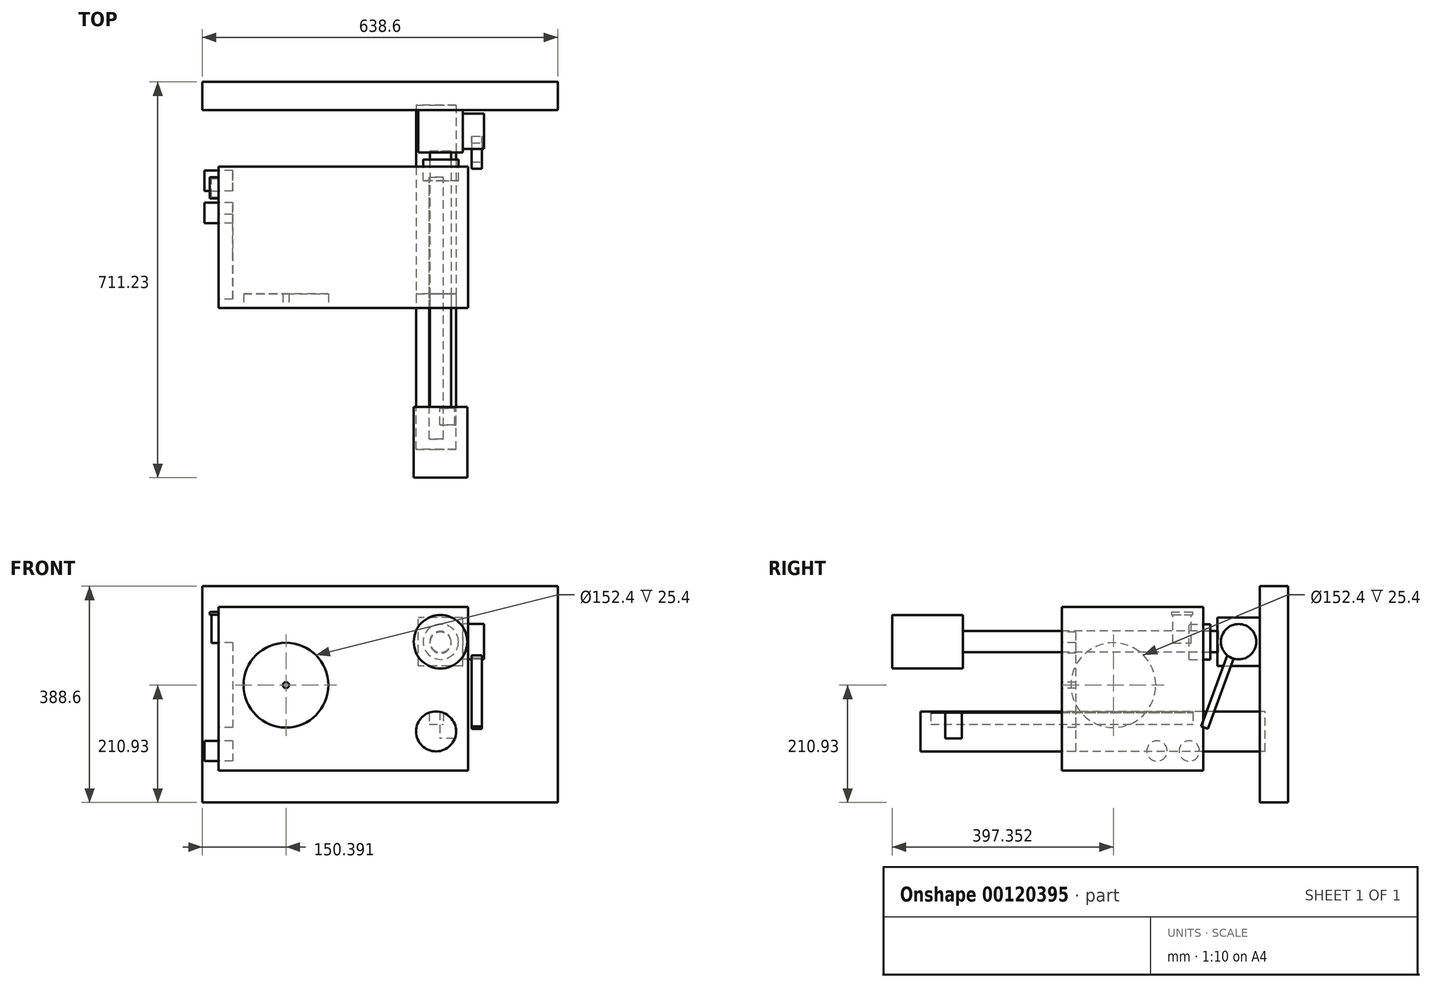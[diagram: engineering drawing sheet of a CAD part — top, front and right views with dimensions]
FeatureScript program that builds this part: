
annotation { "Feature Type Name" : "Feature", "Feature Type Description" : "" }
export const myFeature = defineFeature(function(context is Context, id is Id, definition is map)
    precondition{}
    {
        {
            var Q0;
            Q0=qCreatedBy(makeId("Front.planeOp"),FACE);
            var sketch = newSketch(context, id + "F0", { "sketchPlane" : qUnion([Q0])});
            skLineSegment(sketch, "E0.bottom", {"start": v(319.3, -194.3) * mm, "end": v(-319.3, -194.3) * mm});
            skLineSegment(sketch, "E0.top", {"start": v(319.3, 194.3) * mm, "end": v(-319.3, 194.3) * mm});
            skLineSegment(sketch, "E0.left", {"start": v(319.3, -194.3) * mm, "end": v(319.3, 194.3) * mm});
            skLineSegment(sketch, "E0.right", {"start": v(-319.3, -194.3) * mm, "end": v(-319.3, 194.3) * mm});
            skPoint(sketch, "E0.middle", {"position": v(0, 0) * mm});
            skSolve(sketch);
        }
        {
            var Q0;
            Q0 = qSketchRegion(id + "F0", true);
            extrude(context, id + "F1", {"entities" : qUnion([Q0]), "depth" : 50.8 * mm});
        }
        {
            var Q0;
            Q0=makeQuery(id+"F1.opExtrude","CAP_FACE",FACE,{"disambiguationData":[OSD([sQuery(id+"F0.wireOp",EDGE,"E0.bottom"),sQuery(id+"F0.wireOp",EDGE,"E0.top"),sQuery(id+"F0.wireOp",EDGE,"E0.left"),sQuery(id+"F0.wireOp",EDGE,"E0.right")])],"isStart":false});
            var sketch = newSketch(context, id + "F2", { "sketchPlane" : qUnion([Q0])});
            skLineSegment(sketch, "E1.bottom", {"start": v(148.82, 51.23) * mm, "end": v(68.51, 51.23) * mm});
            skLineSegment(sketch, "E1.top", {"start": v(148.82, 137.9) * mm, "end": v(68.51, 137.9) * mm});
            skLineSegment(sketch, "E1.left", {"start": v(148.82, 51.23) * mm, "end": v(148.82, 137.9) * mm});
            skLineSegment(sketch, "E1.right", {"start": v(68.51, 51.23) * mm, "end": v(68.51, 137.9) * mm});
            skPoint(sketch, "E1.middle", {"position": v(108.67, 94.56) * mm});
            skSolve(sketch);
        }
        {
            var Q0;
            Q0 = qSketchRegion(id + "F2", true);
            extrude(context, id + "F3", {"entities" : qUnion([Q0]), "operationType" : NewBodyOperationType.ADD, "depth" : 76.2 * mm});
        }
        {
            var Q0;
            Q0=makeQuery(id+"F3.opExtrude","SWEPT_FACE",FACE,{"disambiguationData":[OSD([sQuery(id+"F2.wireOp",EDGE,"E1.left")])]});
            var sketch = newSketch(context, id + "F4", { "sketchPlane" : qUnion([Q0])});
            skLineSegment(sketch, "E2", {"start": v(-127, 137.9) * mm, "end": v(-50.8, 51.23) * mm, "construction": true});
            skLineSegment(sketch, "E3", {"start": v(-50.8, 137.9) * mm, "end": v(-127, 51.23) * mm, "construction": true});
            skCircle(sketch, "E4", {"center": v(-88.9, 94.56) * mm, "radius": 31.75 * mm});
            skSolve(sketch);
        }
        {
            var Q0;
            Q0 = qSketchRegion(id + "F4", true);
            extrude(context, id + "F5", {"entities" : qUnion([Q0]), "operationType" : NewBodyOperationType.ADD, "depth" : 38.1 * mm});
        }
        {
            var Q0;
            Q0=makeQuery(id+"F3.opExtrude","CAP_FACE",FACE,{"disambiguationData":[OSD([sQuery(id+"F2.wireOp",EDGE,"E1.bottom"),sQuery(id+"F2.wireOp",EDGE,"E1.top"),sQuery(id+"F2.wireOp",EDGE,"E1.left"),sQuery(id+"F2.wireOp",EDGE,"E1.right")])],"isStart":false});
            var sketch = newSketch(context, id + "F6", { "sketchPlane" : qUnion([Q0])});
            skLineSegment(sketch, "E5", {"start": v(68.51, 137.9) * mm, "end": v(148.82, 51.23) * mm, "construction": true});
            skLineSegment(sketch, "E6", {"start": v(148.82, 137.9) * mm, "end": v(68.51, 51.23) * mm, "construction": true});
            skCircle(sketch, "E7", {"center": v(108.67, 94.56) * mm, "radius": 19.05 * mm});
            skSolve(sketch);
        }
        {
            var Q0;
            Q0 = qSketchRegion(id + "F6", true);
            extrude(context, id + "F7", {"entities" : qUnion([Q0]), "operationType" : NewBodyOperationType.ADD, "depth" : 25.4 * mm});
        }
        {
            var Q0;
            Q0=makeQuery(id+"F7.opExtrude","CAP_FACE",FACE,{"disambiguationData":[OSD([sQuery(id+"F6.wireOp",EDGE,"E7")])],"isStart":false});
            var sketch = newSketch(context, id + "F8", { "sketchPlane" : qUnion([Q0])});
            skLineSegment(sketch, "E8.bottom", {"start": v(158.58, 157.17) * mm, "end": v(-289.75, 157.17) * mm});
            skLineSegment(sketch, "E8.top", {"start": v(158.58, -137.04) * mm, "end": v(-289.75, -137.04) * mm});
            skLineSegment(sketch, "E8.left", {"start": v(158.58, 157.17) * mm, "end": v(158.58, -137.04) * mm});
            skLineSegment(sketch, "E8.right", {"start": v(-289.75, 157.17) * mm, "end": v(-289.75, -137.04) * mm});
            skSolve(sketch);
        }
        {
            var Q0;
            Q0 = qSketchRegion(id + "F8", true);
            extrude(context, id + "F9", {"entities" : qUnion([Q0]), "depth" : 254 * mm});
        }
        {
            var Q0;
            Q0=makeQuery(id+"F9.opExtrude","CAP_FACE",FACE,{"disambiguationData":[OSD([sQuery(id+"F8.wireOp",EDGE,"E8.bottom"),sQuery(id+"F8.wireOp",EDGE,"E8.top"),sQuery(id+"F8.wireOp",EDGE,"E8.left"),sQuery(id+"F8.wireOp",EDGE,"E8.right")])],"isStart":false});
            var sketch = newSketch(context, id + "F10", { "sketchPlane" : qUnion([Q0])});
            skCircle(sketch, "E9", {"center": v(-168.9, 16.63) * mm, "radius": 76.2 * mm});
            skCircle(sketch, "E10", {"center": v(-168.9, 16.63) * mm, "radius": 5.36 * mm});
            skCircle(sketch, "E11", {"center": v(108.84, 92.81) * mm, "radius": 19.05 * mm});
            skCircle(sketch, "E12", {"center": v(100.79, -66.56) * mm, "radius": 35.94 * mm});
            skLineSegment(sketch, "E13.bottom", {"start": v(88.35, -23.15) * mm, "end": v(113.75, -23.15) * mm});
            skLineSegment(sketch, "E13.top", {"start": v(88.35, -53.63) * mm, "end": v(113.75, -53.63) * mm});
            skLineSegment(sketch, "E13.left", {"start": v(88.35, -23.15) * mm, "end": v(88.35, -53.63) * mm});
            skLineSegment(sketch, "E13.right", {"start": v(113.75, -23.15) * mm, "end": v(113.75, -53.63) * mm});
            skSolve(sketch);
        }
        {
            var Q0;
            Q0=makeQuery(id+"F9.opExtrude","SWEPT_FACE",FACE,{"disambiguationData":[OSD([sQuery(id+"F8.wireOp",EDGE,"E8.right")])]});
            var sketch = newSketch(context, id + "F11", { "sketchPlane" : qUnion([Q0])});
            skCircle(sketch, "E14", {"center": v(313.88, 16.63) * mm, "radius": 76.2 * mm});
            skCircle(sketch, "E15", {"center": v(177.56, -101.7) * mm, "radius": 18.33 * mm});
            skCircle(sketch, "E16", {"center": v(235.51, -101.7) * mm, "radius": 18.33 * mm});
            skLineSegment(sketch, "E17", {"start": v(177.56, -101.7) * mm, "end": v(235.51, -101.7) * mm, "construction": true});
            skLineSegment(sketch, "E18.bottom", {"start": v(207.08, 92.5) * mm, "end": v(173.8, 92.5) * mm});
            skLineSegment(sketch, "E18.top", {"start": v(207.08, 143.3) * mm, "end": v(173.8, 143.3) * mm});
            skLineSegment(sketch, "E18.left", {"start": v(207.08, 92.5) * mm, "end": v(207.08, 143.3) * mm});
            skLineSegment(sketch, "E18.right", {"start": v(173.8, 92.5) * mm, "end": v(173.8, 143.3) * mm});
            skSolve(sketch);
        }
        {
            var Q0;
            Q0=makeQuery(id+"F10.imprint","IMPRINT",FACE,{"disambiguationData":[TD([[makeQuery(id+"F10.imprint","IMPRINT",EDGE,{"derivedFrom":sQuery(id+"F10.wireOp",EDGE,"E11")}),1.0]])]});
            extrude(context, id + "F12", {"entities" : qUnion([Q0]), "operationType" : NewBodyOperationType.REMOVE, "oppositeDirection" : true, "depth" : 25.4 * mm});
        }
        {
            var Q0;
            Q0=makeQuery(id+"F10.imprint","IMPRINT",FACE,{"disambiguationData":[TD([[makeQuery(id+"F10.imprint","IMPRINT",EDGE,{"derivedFrom":sQuery(id+"F10.wireOp",EDGE,"E12")}),1.0]])]});
            extrude(context, id + "F13", {"entities" : qUnion([Q0]), "operationType" : NewBodyOperationType.REMOVE, "oppositeDirection" : true, "depth" : 25.4 * mm});
        }
        {
            var Q0;
            Q0=makeQuery(id+"F10.imprint","IMPRINT",FACE,{"disambiguationData":[TD([[makeQuery(id+"F10.imprint","IMPRINT",EDGE,{"derivedFrom":sQuery(id+"F10.wireOp",EDGE,"E9")}),1.0]])]});
            extrude(context, id + "F14", {"entities" : qUnion([Q0]), "operationType" : NewBodyOperationType.REMOVE, "oppositeDirection" : true, "depth" : 25.4 * mm});
        }
        {
            var Q0;
            Q0=makeQuery(id+"F11.imprint","IMPRINT",FACE,{"disambiguationData":[TD([[makeQuery(id+"F11.imprint","IMPRINT",EDGE,{"derivedFrom":sQuery(id+"F11.wireOp",EDGE,"E14")}),1.0]])]});
            extrude(context, id + "F15", {"entities" : qUnion([Q0]), "operationType" : NewBodyOperationType.REMOVE, "oppositeDirection" : true, "depth" : 25.4 * mm});
        }
        {
            var Q0;
            Q0=makeQuery(id+"F11.imprint","IMPRINT",FACE,{"disambiguationData":[TD([[makeQuery(id+"F11.imprint","IMPRINT",EDGE,{"derivedFrom":sQuery(id+"F11.wireOp",EDGE,"E16")}),1.0]])]});
            extrude(context, id + "F16", {"entities" : qUnion([Q0]), "operationType" : NewBodyOperationType.REMOVE, "oppositeDirection" : true, "depth" : 25.4 * mm});
        }
        {
            var Q0;
            Q0=makeQuery(id+"F11.imprint","IMPRINT",FACE,{"disambiguationData":[TD([[makeQuery(id+"F11.imprint","IMPRINT",EDGE,{"derivedFrom":sQuery(id+"F11.wireOp",EDGE,"E15")}),1.0]])]});
            extrude(context, id + "F17", {"entities" : qUnion([Q0]), "operationType" : NewBodyOperationType.REMOVE, "oppositeDirection" : true, "depth" : 25.4 * mm});
        }
        {
            var Q0;
            Q0=makeQuery(id+"F9.opExtrude","SWEPT_FACE",FACE,{"disambiguationData":[OSD([sQuery(id+"F8.wireOp",EDGE,"E8.left")])]});
            cPlane(context, id + "F18", {"entities" : qUnion([Q0]), "cplaneType" : CPlaneType.OFFSET, "offset" : 50.8 * mm, "oppositeDirection" : true, "width" : 152.4 * mm, "height" : 152.4 * mm});
        }
        {
            var Q0;
            Q0=qCreatedBy(id+"F18.planeOp",FACE);
            var sketch = newSketch(context, id + "F19", { "sketchPlane" : qUnion([Q0])});
            skLineSegment(sketch, "E19", {"start": v(-632.3, 94.42) * mm, "end": v(-124.3, 94.42) * mm, "construction": true});
            skLineSegment(sketch, "E20", {"start": v(-584.23, 94.42) * mm, "end": v(-124.3, 94.42) * mm});
            skLineSegment(sketch, "E21", {"start": v(-154.6, -67.58) * mm, "end": v(-688, -67.58) * mm});
            skLineSegment(sketch, "E22.bottom", {"start": v(-616.2, -28.57) * mm, "end": v(-586.36, -28.57) * mm});
            skLineSegment(sketch, "E22.top", {"start": v(-616.2, -79.37) * mm, "end": v(-586.36, -79.37) * mm});
            skLineSegment(sketch, "E22.left", {"start": v(-616.2, -28.57) * mm, "end": v(-616.2, -79.37) * mm});
            skLineSegment(sketch, "E22.right", {"start": v(-586.36, -28.57) * mm, "end": v(-586.36, -79.37) * mm});
            skSolve(sketch);
        }
        {
            var Q0;
            Q0 = qSketchRegion(id + "F6", true);
            var Q1;
            Q1=sQuery(id+"F19.wireOp",EDGE,"E20");
            sweep(context, id + "F20", {"profiles" : qUnion([Q0]), "path" : qUnion([Q1])});
        }
        {
            var Q0;
            Q0=makeQuery(id+"F10.imprint","IMPRINT",FACE,{"disambiguationData":[TD([[makeQuery(id+"F10.imprint","IMPRINT",EDGE,{"derivedFrom":sQuery(id+"F10.wireOp",EDGE,"E12")}),1.0]])]});
            var Q1;
            Q1=sQuery(id+"F10.wireOp",EDGE,"E12");
            extrude(context, id + "F21", {"entities" : qUnion([Q0]), "surfaceEntities" : qUnion([Q1]), "depth" : 254 * mm});
        }
        {
            var Q0;
            Q0=makeQuery(id+"F10.imprint","IMPRINT",FACE,{"disambiguationData":[TD([[makeQuery(id+"F10.imprint","IMPRINT",EDGE,{"derivedFrom":sQuery(id+"F10.wireOp",EDGE,"E12")}),1.0]])]});
            extrude(context, id + "F22", {"entities" : qUnion([Q0]), "oppositeDirection" : true, "depth" : 364.88 * mm});
        }
        {
            var Q0;
            Q0=makeQuery(id+"F20.opSweep","CAP_FACE",FACE,{"disambiguationData":[OSD([sQuery(id+"F6.wireOp",EDGE,"E7"),sQuery(id+"F19.wireOp",VERTEX,"E20.start")])],"isStart":false});
            var sketch = newSketch(context, id + "F23", { "sketchPlane" : qUnion([Q0])});
            skCircle(sketch, "E23", {"center": v(108.67, 94.56) * mm, "radius": 48.04 * mm});
            skSolve(sketch);
        }
        {
            var Q0;
            Q0 = qSketchRegion(id + "F23", true);
            extrude(context, id + "F24", {"entities" : qUnion([Q0]), "operationType" : NewBodyOperationType.ADD, "depth" : 127 * mm});
        }
        {
            var Q0;
            Q0=makeQuery(id+"F11.imprint","IMPRINT",FACE,{"disambiguationData":[TD([[makeQuery(id+"F11.imprint","IMPRINT",EDGE,{"derivedFrom":sQuery(id+"F11.wireOp",EDGE,"E16")}),1.0]])]});
            var Q1;
            Q1=makeQuery(id+"F11.imprint","IMPRINT",FACE,{"disambiguationData":[TD([[makeQuery(id+"F11.imprint","IMPRINT",EDGE,{"derivedFrom":sQuery(id+"F11.wireOp",EDGE,"E15")}),1.0]])]});
            extrude(context, id + "F25", {"entities" : qUnion([Q0, Q1]), "depth" : 25.4 * mm});
        }
        {
            var Q0;
            Q0=makeQuery(id+"F11.imprint","IMPRINT",FACE,{"disambiguationData":[TD([[makeQuery(id+"F11.imprint","IMPRINT",EDGE,{"derivedFrom":sQuery(id+"F11.wireOp",EDGE,"E15")}),1.0]])]});
            var Q1;
            Q1=makeQuery(id+"F11.imprint","IMPRINT",FACE,{"disambiguationData":[TD([[makeQuery(id+"F11.imprint","IMPRINT",EDGE,{"derivedFrom":sQuery(id+"F11.wireOp",EDGE,"E16")}),1.0]])]});
            var Q2;
            Q2=makeQuery(id+"F11.imprint","IMPRINT",FACE,{"disambiguationData":[TD([[makeQuery(id+"F11.imprint","IMPRINT",EDGE,{"derivedFrom":sQuery(id+"F11.wireOp",EDGE,"E18.bottom")}),-1.0]])]});
            var Q3;
            Q3=sQuery(id+"F11.wireOp",EDGE,"E14");
            extrude(context, id + "F26", {"entities" : qUnion([Q0, Q1, Q2]), "bodyType" : ToolBodyType.SURFACE, "surfaceEntities" : qUnion([Q3]), "depth" : 25.4 * mm});
        }
        {
            var Q0;
            Q0=makeQuery(id+"F10.imprint","IMPRINT",FACE,{"disambiguationData":[TD([[makeQuery(id+"F10.imprint","IMPRINT",EDGE,{"derivedFrom":sQuery(id+"F10.wireOp",EDGE,"E9")}),1.0]])]});
            var Q1;
            Q1=sQuery(id+"F10.wireOp",EDGE,"E9");
            extrude(context, id + "F27", {"entities" : qUnion([Q0]), "bodyType" : ToolBodyType.SURFACE, "surfaceEntities" : qUnion([Q1]), "depth" : 25.4 * mm});
        }
        {
            var Q0;
            Q0=makeQuery(id+"F8.imprint","IMPRINT",FACE,{"disambiguationData":[TD([[makeQuery(id+"F8.imprint","IMPRINT",EDGE,{"derivedFrom":sQuery(id+"F8.wireOp",EDGE,"E8.bottom")}),1.0]])]});
            var sketch = newSketch(context, id + "F28", { "sketchPlane" : qUnion([Q0])});
            skCircle(sketch, "E24", {"center": v(109.18, 94.52) * mm, "radius": 31.75 * mm});
            skSolve(sketch);
        }
        {
            var Q0;
            Q0 = qSketchRegion(id + "F28", true);
            extrude(context, id + "F29", {"entities" : qUnion([Q0]), "depth" : 25.4 * mm});
        }
        {
            var Q0;
            Q0 = qSketchRegion(id + "F28", true);
            extrude(context, id + "F30", {"entities" : qUnion([Q0]), "oppositeDirection" : true, "depth" : 12.7 * mm});
        }
        {
            var Q0;
            Q0=makeQuery(id+"F11.imprint","IMPRINT",FACE,{"disambiguationData":[TD([[makeQuery(id+"F11.imprint","IMPRINT",EDGE,{"derivedFrom":sQuery(id+"F11.wireOp",EDGE,"E18.bottom")}),-1.0]])]});
            extrude(context, id + "F31", {"entities" : qUnion([Q0]), "operationType" : NewBodyOperationType.ADD, "depth" : 12.7 * mm});
        }
        {
            var Q0;
            Q0=makeQuery(id+"F31.opExtrude","SWEPT_FACE",FACE,{"disambiguationData":[OSD([sQuery(id+"F11.wireOp",EDGE,"E18.top")])]});
            var sketch = newSketch(context, id + "F32", { "sketchPlane" : qUnion([Q0])});
            skLineSegment(sketch, "E25", {"start": v(-302.45, -173.8) * mm, "end": v(-289.75, -207.08) * mm, "construction": true});
            skLineSegment(sketch, "E26", {"start": v(-289.75, -173.8) * mm, "end": v(-302.45, -207.08) * mm, "construction": true});
            skLineSegment(sketch, "E27.bottom", {"start": v(-305.81, -171.58) * mm, "end": v(-289.75, -171.58) * mm});
            skLineSegment(sketch, "E27.top", {"start": v(-305.81, -209.68) * mm, "end": v(-289.75, -209.68) * mm});
            skLineSegment(sketch, "E27.left", {"start": v(-305.81, -171.58) * mm, "end": v(-305.81, -209.68) * mm});
            skLineSegment(sketch, "E27.right", {"start": v(-289.75, -171.58) * mm, "end": v(-289.75, -209.68) * mm});
            skLineSegment(sketch, "E28", {"start": v(-305.81, -171.58) * mm, "end": v(-289.75, -209.68) * mm, "construction": true});
            skLineSegment(sketch, "E29", {"start": v(-305.81, -209.68) * mm, "end": v(-289.75, -171.58) * mm, "construction": true});
            skSolve(sketch);
        }
        {
            var Q0;
            {var subQ1=sQuery(id+"F11.wireOp",EDGE,"E18.top");Q0=makeQuery(id+"F32.imprint","IMPRINT",FACE,{"disambiguationData":[TD([[makeQuery(id+"F32.imprint","IMPRINT",EDGE,{"derivedFrom":makeQuery(id+"F31.opExtrude","CAP_EDGE",EDGE,{"disambiguationData":[OSD([subQ1])],"isStart":false})}),-1.0]])]});}
            var Q1;
            {var subQ5=sQuery(id+"F32.wireOp",EDGE,"E27.bottom");Q1=makeQuery(id+"F32.imprint","IMPRINT",FACE,{"disambiguationData":[TD([[makeQuery(id+"F32.imprint","IMPRINT",EDGE,{"derivedFrom":subQ5}),-1.0]])]});}
            extrude(context, id + "F33", {"entities" : qUnion([Q0, Q1]), "depth" : 5.08 * mm});
        }
        {
            var Q0;
            Q0=makeQuery(id+"F2.imprint","IMPRINT",FACE,{"disambiguationData":[TD([[makeQuery(id+"F2.imprint","IMPRINT",EDGE,{"derivedFrom":sQuery(id+"F2.wireOp",EDGE,"E1.bottom")}),1.0]])]});
            cPlane(context, id + "F34", {"entities" : qUnion([Q0]), "cplaneType" : CPlaneType.OFFSET, "offset" : 38.1 * mm, "width" : 152.4 * mm, "height" : 152.4 * mm});
        }
        {
            var Q0;
            {var subQ5=sQuery(id+"F10.wireOp",EDGE,"E13.top");Q0=makeQuery(id+"F10.imprint","IMPRINT",FACE,{"disambiguationData":[TD([[makeQuery(id+"F10.imprint","IMPRINT",EDGE,{"derivedFrom":subQ5}),1.0]])]});}
            extrude(context, id + "F35", {"entities" : qUnion([Q0]), "endBound" : BoundingType.SYMMETRIC, "depth" : 470.75 * mm});
        }
        {
            var Q0;
            Q0=makeQuery(id+"F9.opExtrude","SWEPT_FACE",FACE,{"disambiguationData":[OSD([sQuery(id+"F8.wireOp",EDGE,"E8.bottom")])]});
            cPlane(context, id + "F36", {"entities" : qUnion([Q0]), "cplaneType" : CPlaneType.OFFSET, "offset" : 63.5 * mm, "oppositeDirection" : true, "width" : 152.4 * mm, "height" : 152.4 * mm});
        }
        {
            var Q0;
            Q0=qCreatedBy(id+"F36.planeOp",FACE);
            var sketch = newSketch(context, id + "F37", { "sketchPlane" : qUnion([Q0])});
            skCircle(sketch, "E30", {"center": v(101.39, -600.75) * mm, "radius": 10.65 * mm});
            skSolve(sketch);
        }
        {
            var Q0;
            Q0=sQuery(id+"F37.wireOp",EDGE,"E30");
            extrude(context, id + "F38", {"bodyType" : ToolBodyType.SURFACE, "surfaceEntities" : qUnion([Q0]), "oppositeDirection" : true, "depth" : 152.4 * mm});
        }
        {
            var Q0;
            Q0=makeQuery(id+"F3.opExtrude","SWEPT_FACE",FACE,{"disambiguationData":[OSD([sQuery(id+"F2.wireOp",EDGE,"E1.bottom")])]});
            cPlane(context, id + "F39", {"entities" : qUnion([Q0]), "cplaneType" : CPlaneType.OFFSET, "offset" : 25.4 * mm, "oppositeDirection" : true, "width" : 152.4 * mm, "height" : 152.4 * mm});
        }
        {
            var Q0;
            Q0=makeQuery(id+"F1.opExtrude","CAP_FACE",FACE,{"disambiguationData":[OSD([sQuery(id+"F0.wireOp",EDGE,"E0.bottom"),sQuery(id+"F0.wireOp",EDGE,"E0.top"),sQuery(id+"F0.wireOp",EDGE,"E0.left"),sQuery(id+"F0.wireOp",EDGE,"E0.right")])],"isStart":false});
            var Q1;
            Q1=makeQuery(id+"F1.opExtrude","CAP_EDGE",EDGE,{"disambiguationData":[OSD([sQuery(id+"F0.wireOp",EDGE,"E0.top")])],"isStart":false});
            cPlane(context, id + "F40", {"entities" : qUnion([Q0, Q1]), "cplaneType" : CPlaneType.LINE_ANGLE, "offset" : 25.4 * mm, "angle" : 20 * degree, "width" : 152.4 * mm, "height" : 152.4 * mm});
        }
        {
            var Q0;
            Q0=qCreatedBy(id+"F40.planeOp",FACE);
            var sketch = newSketch(context, id + "F41", { "sketchPlane" : qUnion([Q0])});
            skLineSegment(sketch, "E31.bottom", {"start": v(-164.72, 28.36) * mm, "end": v(-183.02, 28.36) * mm});
            skLineSegment(sketch, "E31.top", {"start": v(-164.72, -107.56) * mm, "end": v(-183.02, -107.56) * mm});
            skLineSegment(sketch, "E31.left", {"start": v(-164.72, 28.36) * mm, "end": v(-164.72, -107.56) * mm});
            skLineSegment(sketch, "E31.right", {"start": v(-183.02, 28.36) * mm, "end": v(-183.02, -107.56) * mm});
            skSolve(sketch);
        }
        {
            var Q0;
            Q0 = qSketchRegion(id + "F41", true);
            extrude(context, id + "F42", {"entities" : qUnion([Q0]), "oppositeDirection" : true, "depth" : 12.7 * mm});
        }
        {
            var Q0;
            Q0 = qSketchRegion(id + "F19", true);
            var Q1;
            Q1=makeQuery(id+"F21.opExtrude","SWEPT_FACE",FACE,{"disambiguationData":[OSD([sQuery(id+"F10.wireOp",EDGE,"E12")])]});
            extrude(context, id + "F43", {"entities" : qUnion([Q0]), "endBound" : BoundingType.UP_TO_SURFACE, "endBoundEntityFace" : qUnion([Q1]), "depth" : 30.48 * mm});
        }
        {
            var Q0;
            Q0=makeQuery(id+"F9.opExtrude","SWEPT_FACE",FACE,{"disambiguationData":[OSD([sQuery(id+"F8.wireOp",EDGE,"E8.top")])]});
            cPlane(context, id + "F44", {"entities" : qUnion([Q0]), "cplaneType" : CPlaneType.OFFSET, "offset" : 38.1 * mm, "oppositeDirection" : true, "width" : 152.4 * mm, "height" : 152.4 * mm});
        }
        {
            var Q0;
            Q0=makeQuery(id+"F25.opExtrude","CAP_FACE",FACE,{"disambiguationData":[OSD([sQuery(id+"F11.wireOp",EDGE,"E16")])],"isStart":false});
            cPlane(context, id + "F45", {"entities" : qUnion([Q0]), "cplaneType" : CPlaneType.OFFSET, "offset" : 0 * mm, "width" : 152.4 * mm, "height" : 152.4 * mm});
        }
    });
